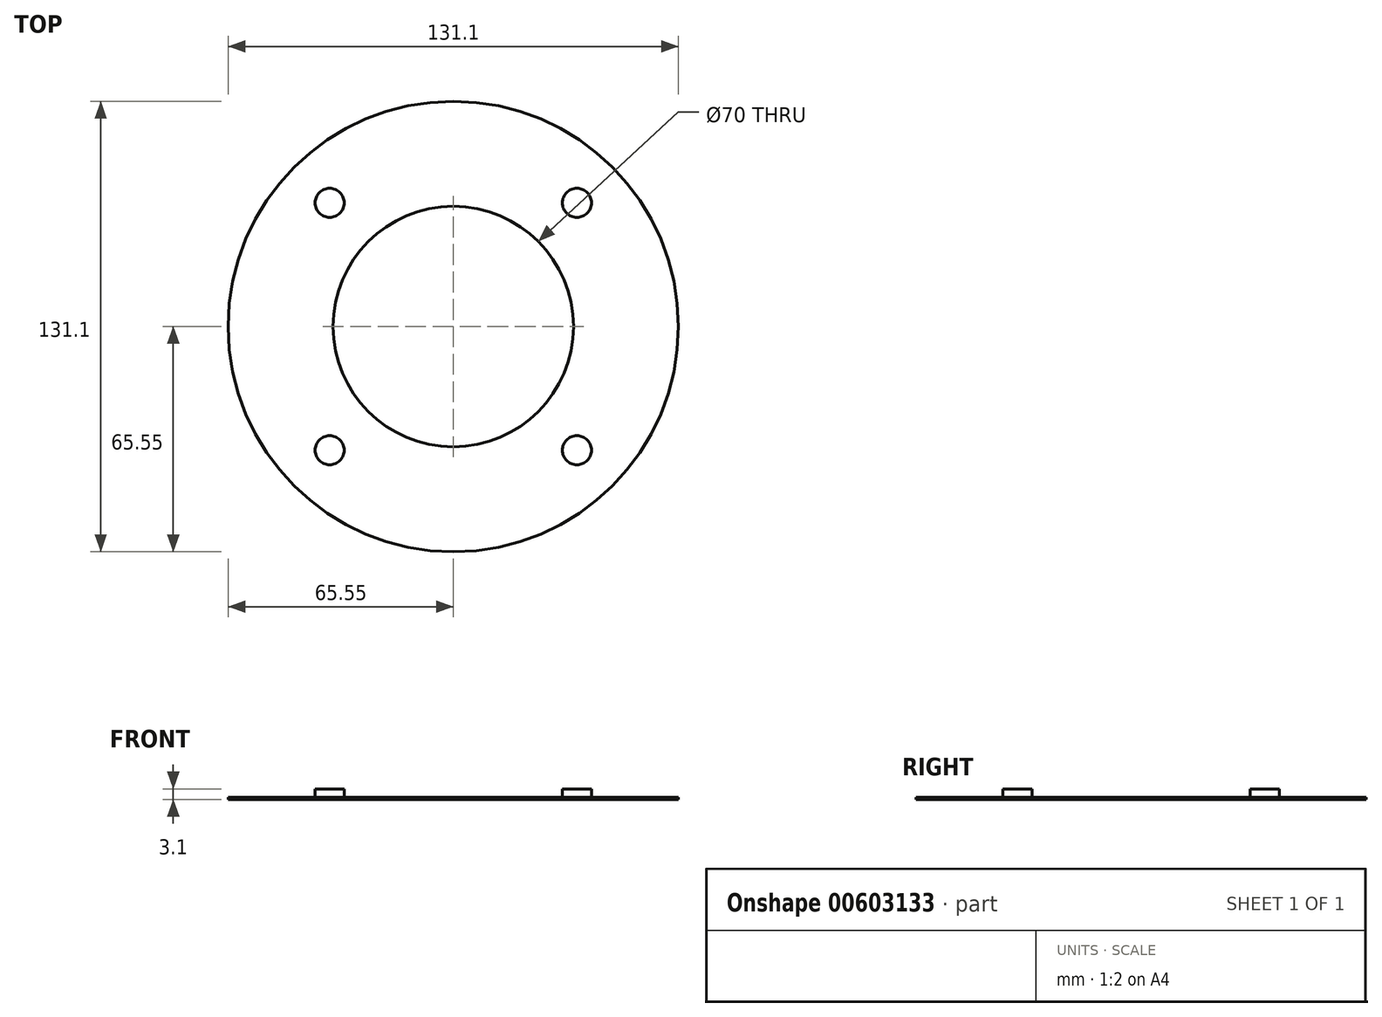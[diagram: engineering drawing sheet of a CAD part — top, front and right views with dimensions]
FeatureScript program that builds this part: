
annotation { "Feature Type Name" : "Feature", "Feature Type Description" : "" }
export const myFeature = defineFeature(function(context is Context, id is Id, definition is map)
    precondition{}
    {
        {
            var Q0;
            Q0=qCreatedBy(makeId("Top.planeOp"),FACE);
            var sketch = newSketch(context, id + "F0", { "sketchPlane" : qUnion([Q0])});
            skCircle(sketch, "E0", {"center": v(0, 0) * mm, "radius": 65.55 * mm});
            skSolve(sketch);
        }
        {
            var Q0;
            Q0 = qSketchRegion(id + "F0", true);
            extrude(context, id + "F1", {"entities" : qUnion([Q0]), "depth" : .6 * mm, "offsetDistance" : 25 * mm});
        }
        {
            var Q0;
            Q0=makeQuery(id+"F1.opExtrude","CAP_FACE",FACE,{"disambiguationData":[OSD([sQuery(id+"F0.wireOp",EDGE,"E0")])],"isStart":false});
            var sketch = newSketch(context, id + "F2", { "sketchPlane" : qUnion([Q0])});
            skCircle(sketch, "E1", {"center": v(-36, 36) * mm, "radius": 4.25 * mm});
            skCircle(sketch, "E2", {"center": v(36, 36) * mm, "radius": 4.25 * mm});
            skCircle(sketch, "E3", {"center": v(36, -36) * mm, "radius": 4.25 * mm});
            skCircle(sketch, "E4", {"center": v(-36, -36) * mm, "radius": 4.25 * mm});
            skLineSegment(sketch, "E5", {"start": v(-36, 36) * mm, "end": v(-36, -36) * mm, "construction": true});
            skLineSegment(sketch, "E6", {"start": v(-36, 36) * mm, "end": v(36, -36) * mm, "construction": true});
            skLineSegment(sketch, "E7", {"start": v(36, 36) * mm, "end": v(0, 0) * mm, "construction": true});
            skLineSegment(sketch, "E8.trimOffspring", {"start": v(-33, -33) * mm, "end": v(-36, -36) * mm, "construction": true});
            skLineSegment(sketch, "E9", {"start": v(-36, 36) * mm, "end": v(36, 36) * mm, "construction": true});
            skSolve(sketch);
        }
        {
            var Q0;
            Q0 = qSketchRegion(id + "F2", true);
            extrude(context, id + "F3", {"entities" : qUnion([Q0]), "operationType" : NewBodyOperationType.ADD, "depth" : 2.5 * mm, "offsetDistance" : 25 * mm});
        }
        {
            var Q0;
            Q0=makeQuery(id+"F1.opExtrude","CAP_FACE",FACE,{"disambiguationData":[OSD([sQuery(id+"F0.wireOp",EDGE,"E0")])],"isStart":false});
            var sketch = newSketch(context, id + "F4", { "sketchPlane" : qUnion([Q0])});
            skCircle(sketch, "E10", {"center": v(0, 0) * mm, "radius": 35 * mm});
            skSolve(sketch);
        }
        {
            var Q0;
            Q0 = qSketchRegion(id + "F4", true);
            extrude(context, id + "F5", {"entities" : qUnion([Q0]), "operationType" : NewBodyOperationType.REMOVE, "endBound" : BoundingType.THROUGH_ALL, "oppositeDirection" : true, "depth" : 25 * mm, "offsetDistance" : 25 * mm});
        }
    });
